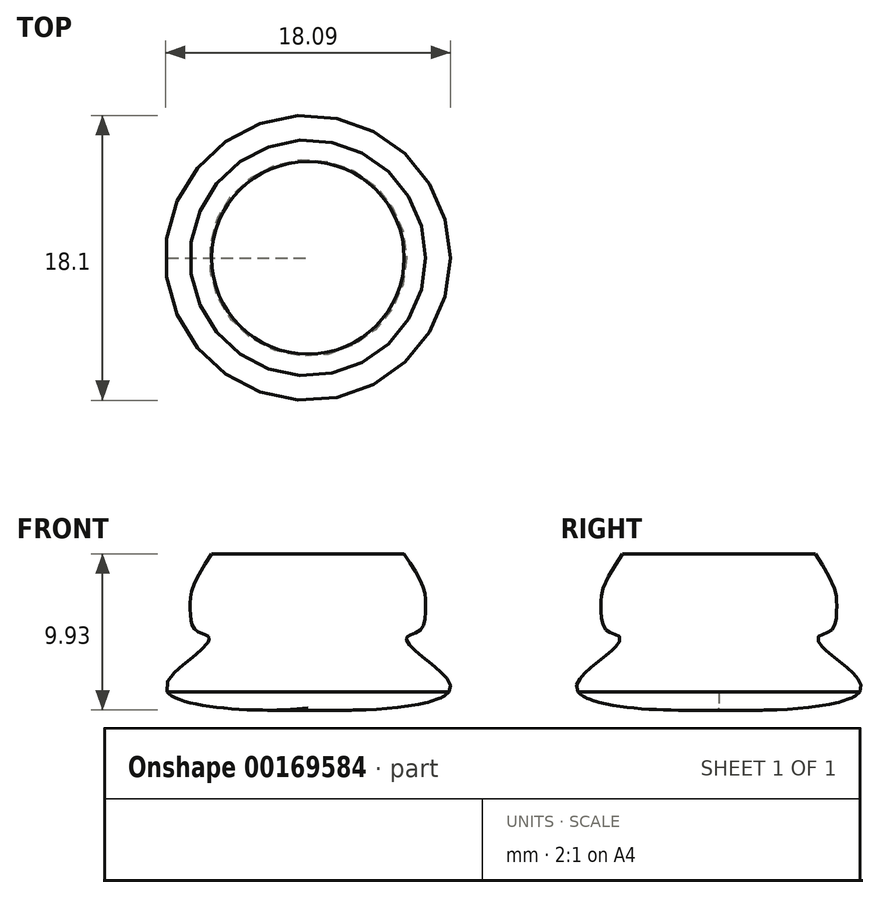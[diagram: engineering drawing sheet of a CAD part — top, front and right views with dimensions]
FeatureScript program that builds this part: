
annotation { "Feature Type Name" : "Feature", "Feature Type Description" : "" }
export const myFeature = defineFeature(function(context is Context, id is Id, definition is map)
    precondition{}
    {
        {
            var Q0;
            Q0=qCreatedBy(makeId("Front.planeOp"),FACE);
            var sketch = newSketch(context, id + "F0", { "sketchPlane" : qUnion([Q0])});
            skLineSegment(sketch, "E0.left", {"start": v(0, 42.86) * mm, "end": v(0, 38.2) * mm});
            skPoint(sketch, "E1.orphan", {"position": v(0, 46.2) * mm});
            skFitSpline(sketch, "E2", {"points": [v(-5, 38.2) * mm, v(-5, 36.1) * mm, v(-4.18, 35.16) * mm, v(-5.79, 26.78) * mm, v(-6.38, 26.1) * mm, v(-5.54, 25.6) * mm, v(-5.45, 24.24) * mm, v(-7.23, 21.1) * mm, v(-7.48, 19.59) * mm, v(-7.14, 18.15) * mm, v(-6.3, 17.73) * mm, v(-6.97, 16.71) * mm, v(-9, 14.3) * mm, v(0, 13.22) * mm], "startDerivative": vector(-4, -17.38) * mm, "endDerivative": vector(48.53, 7.54) * mm});
            skLineSegment(sketch, "E3", {"start": v(-8.96, 14.24) * mm, "end": v(0, 14.2) * mm});
            skLineSegment(sketch, "E4", {"start": v(0, 23) * mm, "end": v(0, 13.22) * mm});
            skPoint(sketch, "E5.orphan", {"position": v(216.1, 13.22) * mm});
            skPoint(sketch, "E0.bottom.end.orphan", {"position": v(-5, 46.2) * mm});
            skLineSegment(sketch, "E6", {"start": v(-6.12, 23) * mm, "end": v(0, 23) * mm});
            skPoint(sketch, "E7.orphan", {"position": v(0, 26.52) * mm});
            skPoint(sketch, "E8.end.orphan", {"position": v(0, 27.77) * mm});
            skPoint(sketch, "E9.orphan", {"position": v(-5.3, 27.77) * mm});
            skSolve(sketch);
        }
        {
            var Q0;
            Q0=qCreatedBy(makeId("Front.planeOp"),FACE);
            var sketch = newSketch(context, id + "F1", { "sketchPlane" : qUnion([Q0])});
            skLineSegment(sketch, "E10", {"start": v(0, 42.86) * mm, "end": v(0, 13.5) * mm});
            skSolve(sketch);
        }
        {
            var Q0;
            Q0=qSketchRegion(id+"F0",true);
            var Q1;
            Q1=sQuery(id+"F1.wireOp",EDGE,"E10");
            revolve(context, id + "F2", {"entities" : qUnion([Q0]), "axis" : qUnion([Q1]), "revolveType" : RevolveType.FULL});
        }
    });
